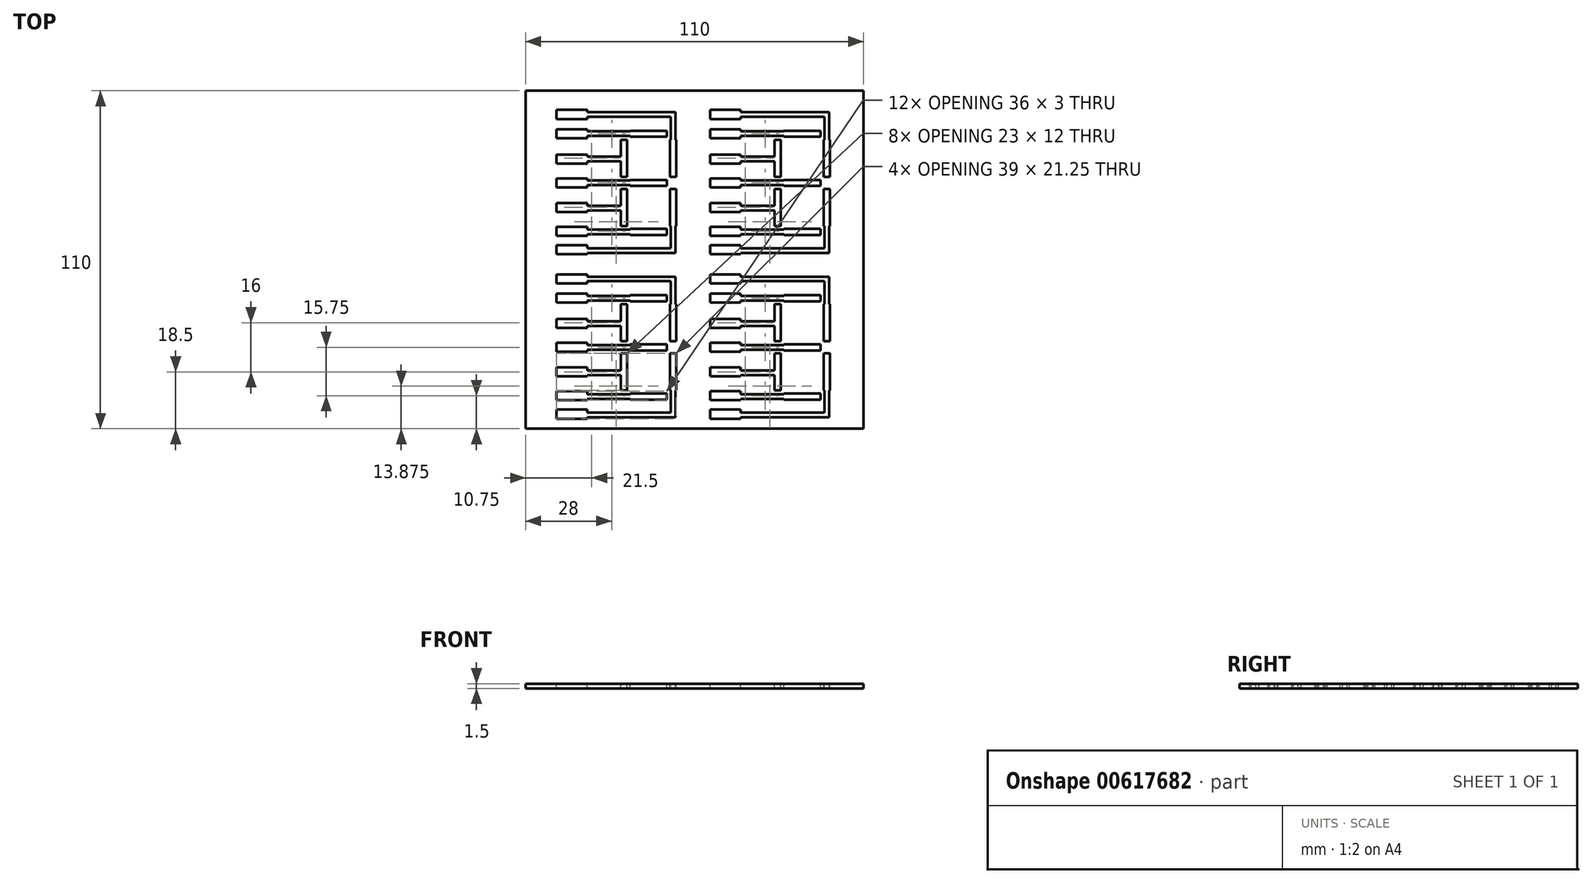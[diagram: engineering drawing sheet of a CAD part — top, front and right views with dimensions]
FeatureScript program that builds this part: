
annotation { "Feature Type Name" : "Feature", "Feature Type Description" : "" }
export const myFeature = defineFeature(function(context is Context, id is Id, definition is map)
    precondition{}
    {
        {
            var Q0;
            Q0=qCreatedBy(makeId("Top.planeOp"),FACE);
            var sketch = newSketch(context, id + "F0", { "sketchPlane" : qUnion([Q0])});
            skLineSegment(sketch, "E0.bottom", {"start": v(0, 0) * mm, "end": v(110, 0) * mm});
            skLineSegment(sketch, "E0.top", {"start": v(0, 110) * mm, "end": v(110, 110) * mm});
            skLineSegment(sketch, "E0.left", {"start": v(0, 0) * mm, "end": v(0, 110) * mm});
            skLineSegment(sketch, "E0.right", {"start": v(110, 0) * mm, "end": v(110, 110) * mm});
            skSolve(sketch);
        }
        {
            var Q0;
            Q0=qSketchRegion(id+"F0",true);
            extrude(context, id + "F1", {"entities" : qUnion([Q0]), "depth" : 1.5 * mm, "offsetDistance" : 25 * mm});
        }
        {
            var Q0;
            Q0=makeQuery(id+"F1.opExtrude","CAP_FACE",FACE,{"disambiguationData":[OSD([sQuery(id+"F0.wireOp",EDGE,"E0.bottom"),sQuery(id+"F0.wireOp",EDGE,"E0.top"),sQuery(id+"F0.wireOp",EDGE,"E0.left"),sQuery(id+"F0.wireOp",EDGE,"E0.right")])],"isStart":false});
            var sketch = newSketch(context, id + "F2", { "sketchPlane" : qUnion([Q0])});
            skLineSegment(sketch, "E1", {"start": v(50, 110) * mm, "end": v(50, 0) * mm, "construction": true});
            skLineSegment(sketch, "E2", {"start": v(100, 110) * mm, "end": v(100, 0) * mm, "construction": true});
            skLineSegment(sketch, "E3", {"start": v(0, 60) * mm, "end": v(110, 60) * mm, "construction": true});
            skLineSegment(sketch, "E4", {"start": v(0, 10) * mm, "end": v(110, 10) * mm, "construction": true});
            skSolve(sketch);
        }
        {
            var Q0;
            Q0=makeQuery(id+"F2.imprint","IMPRINT",FACE,{"disambiguationData":[TD([[makeQuery(id+"F2.imprint","IMPRINT",EDGE,{"derivedFrom":makeQuery(id+"F1.opExtrude","CAP_EDGE",EDGE,{"disambiguationData":[OSD([sQuery(id+"F0.wireOp",EDGE,"E0.bottom")])],"isStart":false})}),1.0]])]});
            var sketch = newSketch(context, id + "F3", { "sketchPlane" : qUnion([Q0])});
            skLineSegment(sketch, "E5.bottom", {"start": v(34, 97) * mm, "end": v(46, 97) * mm});
            skLineSegment(sketch, "E5.top", {"start": v(34, 95) * mm, "end": v(46, 95) * mm});
            skLineSegment(sketch, "E5.left", {"start": v(34, 97) * mm, "end": v(34, 96.75) * mm});
            skLineSegment(sketch, "E5.right", {"start": v(46, 97) * mm, "end": v(46, 95) * mm});
            skLineSegment(sketch, "E6.bottom", {"start": v(47, 94) * mm, "end": v(49, 94) * mm});
            skLineSegment(sketch, "E6.top", {"start": v(47, 82) * mm, "end": v(49, 82) * mm});
            skLineSegment(sketch, "E6.left", {"start": v(47, 94) * mm, "end": v(47, 82) * mm});
            skLineSegment(sketch, "E6.right", {"start": v(49, 94) * mm, "end": v(49, 82) * mm});
            skLineSegment(sketch, "E7.bottom", {"start": v(46, 81) * mm, "end": v(34, 81) * mm});
            skLineSegment(sketch, "E7.top", {"start": v(46, 79) * mm, "end": v(34, 79) * mm});
            skLineSegment(sketch, "E7.left", {"start": v(46, 81) * mm, "end": v(46, 79) * mm});
            skLineSegment(sketch, "E8.bottom", {"start": v(47, 78) * mm, "end": v(49, 78) * mm});
            skLineSegment(sketch, "E8.top", {"start": v(47, 66) * mm, "end": v(47.25, 66) * mm});
            skLineSegment(sketch, "E8.left", {"start": v(47, 78) * mm, "end": v(47, 66) * mm});
            skLineSegment(sketch, "E8.right", {"start": v(49, 78) * mm, "end": v(49, 66) * mm});
            skLineSegment(sketch, "E9.bottom", {"start": v(46, 65) * mm, "end": v(34, 65) * mm});
            skLineSegment(sketch, "E9.top", {"start": v(46, 63) * mm, "end": v(34, 63) * mm});
            skLineSegment(sketch, "E9.left", {"start": v(46, 65) * mm, "end": v(46, 63) * mm});
            skLineSegment(sketch, "E9.right", {"start": v(34, 65) * mm, "end": v(34, 64.75) * mm});
            skLineSegment(sketch, "E10.bottom", {"start": v(33, 66) * mm, "end": v(31, 66) * mm});
            skLineSegment(sketch, "E10.top", {"start": v(33, 78) * mm, "end": v(31, 78) * mm});
            skLineSegment(sketch, "E10.left", {"start": v(33, 66) * mm, "end": v(33, 78) * mm});
            skLineSegment(sketch, "E10.right", {"start": v(31, 66) * mm, "end": v(31, 71) * mm});
            skLineSegment(sketch, "E11.bottom", {"start": v(33, 82) * mm, "end": v(31, 82) * mm});
            skLineSegment(sketch, "E11.top", {"start": v(33, 94) * mm, "end": v(31, 94) * mm});
            skLineSegment(sketch, "E11.left", {"start": v(33, 82) * mm, "end": v(33, 94) * mm});
            skLineSegment(sketch, "E11.right", {"start": v(31, 82) * mm, "end": v(31, 87) * mm});
            skLineSegment(sketch, "E12", {"start": v(48.75, 94) * mm, "end": v(48.75, 103) * mm});
            skLineSegment(sketch, "E13", {"start": v(48.75, 103) * mm, "end": v(20, 103) * mm});
            skLineSegment(sketch, "E14", {"start": v(47.25, 94) * mm, "end": v(47.25, 101.5) * mm});
            skLineSegment(sketch, "E15", {"start": v(47.25, 101.5) * mm, "end": v(20, 101.5) * mm});
            skLineSegment(sketch, "E16", {"start": v(20, 101.5) * mm, "end": v(20, 100.75) * mm});
            skLineSegment(sketch, "E17", {"start": v(20, 100.75) * mm, "end": v(10, 100.75) * mm});
            skLineSegment(sketch, "E18", {"start": v(10, 100.75) * mm, "end": v(10, 103.75) * mm});
            skLineSegment(sketch, "E19", {"start": v(10, 103.75) * mm, "end": v(20, 103.75) * mm});
            skLineSegment(sketch, "E20", {"start": v(20, 103.75) * mm, "end": v(20, 103) * mm});
            skLineSegment(sketch, "E21", {"start": v(34, 96.75) * mm, "end": v(20, 96.75) * mm});
            skLineSegment(sketch, "E22", {"start": v(20, 96.75) * mm, "end": v(20, 97.5) * mm});
            skLineSegment(sketch, "E23", {"start": v(20, 97.5) * mm, "end": v(10, 97.5) * mm});
            skLineSegment(sketch, "E24", {"start": v(10, 97.5) * mm, "end": v(10, 94.5) * mm});
            skLineSegment(sketch, "E25", {"start": v(10, 94.5) * mm, "end": v(20, 94.5) * mm});
            skLineSegment(sketch, "E26.trimOffspring", {"start": v(34, 95.25) * mm, "end": v(34, 95) * mm});
            skLineSegment(sketch, "E27.bottom", {"start": v(31, 88.5) * mm, "end": v(20, 88.5) * mm});
            skLineSegment(sketch, "E27.top", {"start": v(31, 87) * mm, "end": v(20, 87) * mm});
            skLineSegment(sketch, "E28.bottom", {"start": v(20, 89.25) * mm, "end": v(10, 89.25) * mm});
            skLineSegment(sketch, "E28.top", {"start": v(20, 86.25) * mm, "end": v(10, 86.25) * mm});
            skLineSegment(sketch, "E28.left", {"start": v(20, 89.25) * mm, "end": v(20, 88.5) * mm});
            skLineSegment(sketch, "E28.right", {"start": v(10, 89.25) * mm, "end": v(10, 86.25) * mm});
            skLineSegment(sketch, "E29.trimOffspring", {"start": v(20, 87) * mm, "end": v(20, 86.25) * mm});
            skLineSegment(sketch, "E30.trimOffspring", {"start": v(31, 88.5) * mm, "end": v(31, 94) * mm});
            skLineSegment(sketch, "E31.bottom", {"start": v(34, 80.75) * mm, "end": v(20, 80.75) * mm});
            skLineSegment(sketch, "E31.top", {"start": v(34, 79.25) * mm, "end": v(20, 79.25) * mm});
            skLineSegment(sketch, "E32.bottom", {"start": v(20, 81.5) * mm, "end": v(10, 81.5) * mm});
            skLineSegment(sketch, "E32.top", {"start": v(20, 78.5) * mm, "end": v(10, 78.5) * mm});
            skLineSegment(sketch, "E32.left", {"start": v(20, 81.5) * mm, "end": v(20, 80.75) * mm});
            skLineSegment(sketch, "E32.right", {"start": v(10, 81.5) * mm, "end": v(10, 78.5) * mm});
            skLineSegment(sketch, "E33.trimOffspring", {"start": v(20, 79.25) * mm, "end": v(20, 78.5) * mm});
            skLineSegment(sketch, "E34.bottom", {"start": v(31, 72.5) * mm, "end": v(20, 72.5) * mm});
            skLineSegment(sketch, "E34.top", {"start": v(31, 71) * mm, "end": v(20, 71) * mm});
            skLineSegment(sketch, "E35.bottom", {"start": v(20, 73.5) * mm, "end": v(10, 73.5) * mm});
            skLineSegment(sketch, "E35.top", {"start": v(20, 70.5) * mm, "end": v(10, 70.5) * mm});
            skLineSegment(sketch, "E35.left", {"start": v(20, 73.5) * mm, "end": v(20, 72.5) * mm});
            skLineSegment(sketch, "E35.right", {"start": v(10, 73.5) * mm, "end": v(10, 70.5) * mm});
            skLineSegment(sketch, "E36.trimOffspring", {"start": v(20, 71) * mm, "end": v(20, 70.5) * mm});
            skLineSegment(sketch, "E37.trimOffspring", {"start": v(31, 72.5) * mm, "end": v(31, 78) * mm});
            skLineSegment(sketch, "E38.trimOffspring", {"start": v(34, 79.25) * mm, "end": v(34, 79) * mm});
            skLineSegment(sketch, "E39.bottom", {"start": v(34, 64.75) * mm, "end": v(20, 64.75) * mm});
            skLineSegment(sketch, "E39.top", {"start": v(34, 63.25) * mm, "end": v(20, 63.25) * mm});
            skLineSegment(sketch, "E40.bottom", {"start": v(20, 65.75) * mm, "end": v(10, 65.75) * mm});
            skLineSegment(sketch, "E40.top", {"start": v(20, 62.75) * mm, "end": v(10, 62.75) * mm});
            skLineSegment(sketch, "E40.left", {"start": v(20, 65.75) * mm, "end": v(20, 64.75) * mm});
            skLineSegment(sketch, "E40.right", {"start": v(10, 65.75) * mm, "end": v(10, 62.75) * mm});
            skLineSegment(sketch, "E41.trimOffspring", {"start": v(20, 63.25) * mm, "end": v(20, 62.75) * mm});
            skLineSegment(sketch, "E42.trimOffspring", {"start": v(34, 63.25) * mm, "end": v(34, 63) * mm});
            skLineSegment(sketch, "E43.bottom", {"start": v(47.25, 58.75) * mm, "end": v(20, 58.75) * mm});
            skLineSegment(sketch, "E43.top", {"start": v(48.75, 57.25) * mm, "end": v(20, 57.25) * mm});
            skLineSegment(sketch, "E44.bottom", {"start": v(20, 59.75) * mm, "end": v(10, 59.75) * mm});
            skLineSegment(sketch, "E44.top", {"start": v(20, 56.75) * mm, "end": v(10, 56.75) * mm});
            skLineSegment(sketch, "E44.left", {"start": v(20, 59.75) * mm, "end": v(20, 58.75) * mm});
            skLineSegment(sketch, "E44.right", {"start": v(10, 59.75) * mm, "end": v(10, 56.75) * mm});
            skLineSegment(sketch, "E45.trimOffspring", {"start": v(20, 57.25) * mm, "end": v(20, 56.75) * mm});
            skLineSegment(sketch, "E46", {"start": v(48.75, 57.25) * mm, "end": v(48.75, 66) * mm});
            skLineSegment(sketch, "E47", {"start": v(47.25, 58.75) * mm, "end": v(47.25, 66) * mm});
            skLineSegment(sketch, "E48.trimOffspring", {"start": v(48.75, 66) * mm, "end": v(49, 66) * mm});
            skLineSegment(sketch, "E49", {"start": v(34, 80.75) * mm, "end": v(34, 81) * mm});
            skLineSegment(sketch, "E50", {"start": v(34, 95.25) * mm, "end": v(20, 95.25) * mm});
            skLineSegment(sketch, "E51", {"start": v(20, 95.25) * mm, "end": v(20, 94.5) * mm});
            skLineSegment(sketch, "E52.0.1.0", {"start": v(10, 44) * mm, "end": v(10, 41) * mm});
            skLineSegment(sketch, "E52.0.1.1", {"start": v(34, 27.25) * mm, "end": v(20, 27.25) * mm});
            skLineSegment(sketch, "E52.0.1.2", {"start": v(31, 19) * mm, "end": v(31, 24.5) * mm});
            skLineSegment(sketch, "E52.0.1.3", {"start": v(47.25, 5.25) * mm, "end": v(20, 5.25) * mm});
            skLineSegment(sketch, "E52.0.1.4", {"start": v(31, 17.5) * mm, "end": v(20, 17.5) * mm});
            skLineSegment(sketch, "E52.0.1.5", {"start": v(20, 17) * mm, "end": v(10, 17) * mm});
            skLineSegment(sketch, "E52.0.1.6", {"start": v(34, 25.75) * mm, "end": v(20, 25.75) * mm});
            skLineSegment(sketch, "E52.0.1.7", {"start": v(31, 19) * mm, "end": v(20, 19) * mm});
            skLineSegment(sketch, "E52.0.1.8", {"start": v(20, 25) * mm, "end": v(10, 25) * mm});
            skLineSegment(sketch, "E52.0.1.9", {"start": v(47, 24.5) * mm, "end": v(47, 12.5) * mm});
            skLineSegment(sketch, "E52.0.1.10", {"start": v(20, 20) * mm, "end": v(10, 20) * mm});
            skLineSegment(sketch, "E52.0.1.11", {"start": v(10, 47.25) * mm, "end": v(10, 50.25) * mm});
            skLineSegment(sketch, "E52.0.1.12", {"start": v(31, 12.5) * mm, "end": v(31, 17.5) * mm});
            skLineSegment(sketch, "E52.0.1.13", {"start": v(10, 12.25) * mm, "end": v(10, 9.25) * mm});
            skLineSegment(sketch, "E52.0.1.14", {"start": v(10, 41) * mm, "end": v(20, 41) * mm});
            skLineSegment(sketch, "E52.0.1.15", {"start": v(10, 50.25) * mm, "end": v(20, 50.25) * mm});
            skLineSegment(sketch, "E52.0.1.16", {"start": v(10, 20) * mm, "end": v(10, 17) * mm});
            skLineSegment(sketch, "E52.0.1.17", {"start": v(34, 9.75) * mm, "end": v(20, 9.75) * mm});
            skLineSegment(sketch, "E52.0.1.18", {"start": v(48.75, 49.5) * mm, "end": v(20, 49.5) * mm});
            skLineSegment(sketch, "E52.0.1.19", {"start": v(34, 41.75) * mm, "end": v(20, 41.75) * mm});
            skLineSegment(sketch, "E52.0.1.20", {"start": v(47.25, 48) * mm, "end": v(20, 48) * mm});
            skLineSegment(sketch, "E52.0.1.21", {"start": v(48.75, 40.5) * mm, "end": v(48.75, 49.5) * mm});
            skLineSegment(sketch, "E52.0.1.22", {"start": v(20, 12.25) * mm, "end": v(10, 12.25) * mm});
            skLineSegment(sketch, "E52.0.1.23", {"start": v(10, 6.25) * mm, "end": v(10, 3.25) * mm});
            skLineSegment(sketch, "E52.0.1.24", {"start": v(33, 28.5) * mm, "end": v(33, 40.5) * mm});
            skLineSegment(sketch, "E52.0.1.25", {"start": v(34, 11.25) * mm, "end": v(20, 11.25) * mm});
            skLineSegment(sketch, "E52.0.1.26", {"start": v(20, 47.25) * mm, "end": v(10, 47.25) * mm});
            skLineSegment(sketch, "E52.0.1.27", {"start": v(20, 9.25) * mm, "end": v(10, 9.25) * mm});
            skLineSegment(sketch, "E52.0.1.28", {"start": v(34, 43.25) * mm, "end": v(20, 43.25) * mm});
            skLineSegment(sketch, "E52.0.1.29", {"start": v(33, 12.5) * mm, "end": v(33, 24.5) * mm});
            skLineSegment(sketch, "E52.0.1.30", {"start": v(47, 40.5) * mm, "end": v(47, 28.5) * mm});
            skLineSegment(sketch, "E52.0.1.31", {"start": v(10, 35.75) * mm, "end": v(10, 32.75) * mm});
            skLineSegment(sketch, "E52.0.1.32", {"start": v(20, 6.25) * mm, "end": v(10, 6.25) * mm});
            skLineSegment(sketch, "E52.0.1.33", {"start": v(34, 43.5) * mm, "end": v(46, 43.5) * mm});
            skLineSegment(sketch, "E52.0.1.34", {"start": v(49, 40.5) * mm, "end": v(49, 28.5) * mm});
            skLineSegment(sketch, "E52.0.1.35", {"start": v(31, 35) * mm, "end": v(20, 35) * mm});
            skLineSegment(sketch, "E52.0.1.36", {"start": v(46, 27.5) * mm, "end": v(34, 27.5) * mm});
            skLineSegment(sketch, "E52.0.1.37", {"start": v(48.75, 3.75) * mm, "end": v(48.75, 12.5) * mm});
            skLineSegment(sketch, "E52.0.1.38", {"start": v(46, 25.5) * mm, "end": v(34, 25.5) * mm});
            skLineSegment(sketch, "E52.0.1.39", {"start": v(31, 33.5) * mm, "end": v(20, 33.5) * mm});
            skLineSegment(sketch, "E52.0.1.40", {"start": v(47.25, 40.5) * mm, "end": v(47.25, 48) * mm});
            skLineSegment(sketch, "E52.0.1.41", {"start": v(48.75, 3.75) * mm, "end": v(20, 3.75) * mm});
            skLineSegment(sketch, "E52.0.1.42", {"start": v(49, 24.5) * mm, "end": v(49, 12.5) * mm});
            skLineSegment(sketch, "E52.0.1.43", {"start": v(10, 28) * mm, "end": v(10, 25) * mm});
            skLineSegment(sketch, "E52.0.1.44", {"start": v(34, 41.5) * mm, "end": v(46, 41.5) * mm});
            skLineSegment(sketch, "E52.0.1.45", {"start": v(20, 28) * mm, "end": v(10, 28) * mm});
            skLineSegment(sketch, "E52.0.1.46", {"start": v(46, 9.5) * mm, "end": v(34, 9.5) * mm});
            skLineSegment(sketch, "E52.0.1.47", {"start": v(20, 3.25) * mm, "end": v(10, 3.25) * mm});
            skLineSegment(sketch, "E52.0.1.48", {"start": v(20, 32.75) * mm, "end": v(10, 32.75) * mm});
            skLineSegment(sketch, "E52.0.1.49", {"start": v(47.25, 5.25) * mm, "end": v(47.25, 12.5) * mm});
            skLineSegment(sketch, "E52.0.1.50", {"start": v(20, 35.75) * mm, "end": v(10, 35.75) * mm});
            skLineSegment(sketch, "E52.0.1.51", {"start": v(46, 11.5) * mm, "end": v(34, 11.5) * mm});
            skLineSegment(sketch, "E52.0.1.52", {"start": v(20, 44) * mm, "end": v(10, 44) * mm});
            skLineSegment(sketch, "E52.0.1.53", {"start": v(31, 35) * mm, "end": v(31, 40.5) * mm});
            skLineSegment(sketch, "E52.0.1.54", {"start": v(31, 28.5) * mm, "end": v(31, 33.5) * mm});
            skLineSegment(sketch, "E52.0.1.55", {"start": v(33, 24.5) * mm, "end": v(31, 24.5) * mm});
            skLineSegment(sketch, "E52.0.1.56", {"start": v(20, 20) * mm, "end": v(20, 19) * mm});
            skLineSegment(sketch, "E52.0.1.57", {"start": v(47, 28.5) * mm, "end": v(49, 28.5) * mm});
            skLineSegment(sketch, "E52.0.1.58", {"start": v(20, 33.5) * mm, "end": v(20, 32.75) * mm});
            skLineSegment(sketch, "E52.0.1.59", {"start": v(20, 6.25) * mm, "end": v(20, 5.25) * mm});
            skLineSegment(sketch, "E52.0.1.60", {"start": v(33, 40.5) * mm, "end": v(31, 40.5) * mm});
            skLineSegment(sketch, "E52.0.1.61", {"start": v(20, 12.25) * mm, "end": v(20, 11.25) * mm});
            skLineSegment(sketch, "E52.0.1.62", {"start": v(47, 24.5) * mm, "end": v(49, 24.5) * mm});
            skLineSegment(sketch, "E52.0.1.63", {"start": v(46, 43.5) * mm, "end": v(46, 41.5) * mm});
            skLineSegment(sketch, "E52.0.1.64", {"start": v(46, 11.5) * mm, "end": v(46, 9.5) * mm});
            skLineSegment(sketch, "E52.0.1.65", {"start": v(46, 27.5) * mm, "end": v(46, 25.5) * mm});
            skLineSegment(sketch, "E52.0.1.66", {"start": v(33, 28.5) * mm, "end": v(31, 28.5) * mm});
            skLineSegment(sketch, "E52.0.1.67", {"start": v(34, 27.25) * mm, "end": v(34, 27.5) * mm});
            skLineSegment(sketch, "E52.0.1.68", {"start": v(34, 43.5) * mm, "end": v(34, 43.25) * mm});
            skLineSegment(sketch, "E52.0.1.69", {"start": v(20, 28) * mm, "end": v(20, 27.25) * mm});
            skLineSegment(sketch, "E52.0.1.70", {"start": v(20, 3.75) * mm, "end": v(20, 3.25) * mm});
            skLineSegment(sketch, "E52.0.1.71", {"start": v(20, 9.75) * mm, "end": v(20, 9.25) * mm});
            skLineSegment(sketch, "E52.0.1.72", {"start": v(20, 50.25) * mm, "end": v(20, 49.5) * mm});
            skLineSegment(sketch, "E52.0.1.73", {"start": v(20, 17.5) * mm, "end": v(20, 17) * mm});
            skLineSegment(sketch, "E52.0.1.74", {"start": v(47, 40.5) * mm, "end": v(49, 40.5) * mm});
            skLineSegment(sketch, "E52.0.1.75", {"start": v(20, 35.75) * mm, "end": v(20, 35) * mm});
            skLineSegment(sketch, "E52.0.1.76", {"start": v(20, 48) * mm, "end": v(20, 47.25) * mm});
            skLineSegment(sketch, "E52.0.1.77", {"start": v(33, 12.5) * mm, "end": v(31, 12.5) * mm});
            skLineSegment(sketch, "E52.0.1.78", {"start": v(20, 43.25) * mm, "end": v(20, 44) * mm});
            skLineSegment(sketch, "E52.0.1.79", {"start": v(48.75, 12.5) * mm, "end": v(49, 12.5) * mm});
            skLineSegment(sketch, "E52.0.1.80", {"start": v(34, 25.75) * mm, "end": v(34, 25.5) * mm});
            skLineSegment(sketch, "E52.0.1.81", {"start": v(47, 12.5) * mm, "end": v(47.25, 12.5) * mm});
            skLineSegment(sketch, "E52.0.1.82", {"start": v(20, 25.75) * mm, "end": v(20, 25) * mm});
            skLineSegment(sketch, "E52.0.1.83", {"start": v(20, 41.75) * mm, "end": v(20, 41) * mm});
            skLineSegment(sketch, "E52.0.1.84", {"start": v(34, 41.75) * mm, "end": v(34, 41.5) * mm});
            skLineSegment(sketch, "E52.0.1.85", {"start": v(34, 11.5) * mm, "end": v(34, 11.25) * mm});
            skLineSegment(sketch, "E52.0.1.86", {"start": v(34, 9.75) * mm, "end": v(34, 9.5) * mm});
            skLineSegment(sketch, "E52.1.0.0", {"start": v(60, 97.5) * mm, "end": v(60, 94.5) * mm});
            skLineSegment(sketch, "E52.1.0.1", {"start": v(84, 80.75) * mm, "end": v(70, 80.75) * mm});
            skLineSegment(sketch, "E52.1.0.2", {"start": v(81, 72.5) * mm, "end": v(81, 78) * mm});
            skLineSegment(sketch, "E52.1.0.3", {"start": v(97.25, 58.75) * mm, "end": v(70, 58.75) * mm});
            skLineSegment(sketch, "E52.1.0.4", {"start": v(81, 71) * mm, "end": v(70, 71) * mm});
            skLineSegment(sketch, "E52.1.0.5", {"start": v(70, 70.5) * mm, "end": v(60, 70.5) * mm});
            skLineSegment(sketch, "E52.1.0.6", {"start": v(84, 79.25) * mm, "end": v(70, 79.25) * mm});
            skLineSegment(sketch, "E52.1.0.7", {"start": v(81, 72.5) * mm, "end": v(70, 72.5) * mm});
            skLineSegment(sketch, "E52.1.0.8", {"start": v(70, 78.5) * mm, "end": v(60, 78.5) * mm});
            skLineSegment(sketch, "E52.1.0.9", {"start": v(97, 78) * mm, "end": v(97, 66) * mm});
            skLineSegment(sketch, "E52.1.0.10", {"start": v(70, 73.5) * mm, "end": v(60, 73.5) * mm});
            skLineSegment(sketch, "E52.1.0.11", {"start": v(60, 100.75) * mm, "end": v(60, 103.75) * mm});
            skLineSegment(sketch, "E52.1.0.12", {"start": v(81, 66) * mm, "end": v(81, 71) * mm});
            skLineSegment(sketch, "E52.1.0.13", {"start": v(60, 65.75) * mm, "end": v(60, 62.75) * mm});
            skLineSegment(sketch, "E52.1.0.14", {"start": v(60, 94.5) * mm, "end": v(70, 94.5) * mm});
            skLineSegment(sketch, "E52.1.0.15", {"start": v(60, 103.75) * mm, "end": v(70, 103.75) * mm});
            skLineSegment(sketch, "E52.1.0.16", {"start": v(60, 73.5) * mm, "end": v(60, 70.5) * mm});
            skLineSegment(sketch, "E52.1.0.17", {"start": v(84, 63.25) * mm, "end": v(70, 63.25) * mm});
            skLineSegment(sketch, "E52.1.0.18", {"start": v(98.75, 103) * mm, "end": v(70, 103) * mm});
            skLineSegment(sketch, "E52.1.0.19", {"start": v(84, 95.25) * mm, "end": v(70, 95.25) * mm});
            skLineSegment(sketch, "E52.1.0.20", {"start": v(97.25, 101.5) * mm, "end": v(70, 101.5) * mm});
            skLineSegment(sketch, "E52.1.0.21", {"start": v(98.75, 94) * mm, "end": v(98.75, 103) * mm});
            skLineSegment(sketch, "E52.1.0.22", {"start": v(70, 65.75) * mm, "end": v(60, 65.75) * mm});
            skLineSegment(sketch, "E52.1.0.23", {"start": v(60, 59.75) * mm, "end": v(60, 56.75) * mm});
            skLineSegment(sketch, "E52.1.0.24", {"start": v(83, 82) * mm, "end": v(83, 94) * mm});
            skLineSegment(sketch, "E52.1.0.25", {"start": v(84, 64.75) * mm, "end": v(70, 64.75) * mm});
            skLineSegment(sketch, "E52.1.0.26", {"start": v(70, 100.75) * mm, "end": v(60, 100.75) * mm});
            skLineSegment(sketch, "E52.1.0.27", {"start": v(70, 62.75) * mm, "end": v(60, 62.75) * mm});
            skLineSegment(sketch, "E52.1.0.28", {"start": v(84, 96.75) * mm, "end": v(70, 96.75) * mm});
            skLineSegment(sketch, "E52.1.0.29", {"start": v(83, 66) * mm, "end": v(83, 78) * mm});
            skLineSegment(sketch, "E52.1.0.30", {"start": v(97, 94) * mm, "end": v(97, 82) * mm});
            skLineSegment(sketch, "E52.1.0.31", {"start": v(60, 89.25) * mm, "end": v(60, 86.25) * mm});
            skLineSegment(sketch, "E52.1.0.32", {"start": v(70, 59.75) * mm, "end": v(60, 59.75) * mm});
            skLineSegment(sketch, "E52.1.0.33", {"start": v(84, 97) * mm, "end": v(96, 97) * mm});
            skLineSegment(sketch, "E52.1.0.34", {"start": v(99, 94) * mm, "end": v(99, 82) * mm});
            skLineSegment(sketch, "E52.1.0.35", {"start": v(81, 88.5) * mm, "end": v(70, 88.5) * mm});
            skLineSegment(sketch, "E52.1.0.36", {"start": v(96, 81) * mm, "end": v(84, 81) * mm});
            skLineSegment(sketch, "E52.1.0.37", {"start": v(98.75, 57.25) * mm, "end": v(98.75, 66) * mm});
            skLineSegment(sketch, "E52.1.0.38", {"start": v(96, 79) * mm, "end": v(84, 79) * mm});
            skLineSegment(sketch, "E52.1.0.39", {"start": v(81, 87) * mm, "end": v(70, 87) * mm});
            skLineSegment(sketch, "E52.1.0.40", {"start": v(97.25, 94) * mm, "end": v(97.25, 101.5) * mm});
            skLineSegment(sketch, "E52.1.0.41", {"start": v(98.75, 57.25) * mm, "end": v(70, 57.25) * mm});
            skLineSegment(sketch, "E52.1.0.42", {"start": v(99, 78) * mm, "end": v(99, 66) * mm});
            skLineSegment(sketch, "E52.1.0.43", {"start": v(60, 81.5) * mm, "end": v(60, 78.5) * mm});
            skLineSegment(sketch, "E52.1.0.44", {"start": v(84, 95) * mm, "end": v(96, 95) * mm});
            skLineSegment(sketch, "E52.1.0.45", {"start": v(70, 81.5) * mm, "end": v(60, 81.5) * mm});
            skLineSegment(sketch, "E52.1.0.46", {"start": v(96, 63) * mm, "end": v(84, 63) * mm});
            skLineSegment(sketch, "E52.1.0.47", {"start": v(70, 56.75) * mm, "end": v(60, 56.75) * mm});
            skLineSegment(sketch, "E52.1.0.48", {"start": v(70, 86.25) * mm, "end": v(60, 86.25) * mm});
            skLineSegment(sketch, "E52.1.0.49", {"start": v(97.25, 58.75) * mm, "end": v(97.25, 66) * mm});
            skLineSegment(sketch, "E52.1.0.50", {"start": v(70, 89.25) * mm, "end": v(60, 89.25) * mm});
            skLineSegment(sketch, "E52.1.0.51", {"start": v(96, 65) * mm, "end": v(84, 65) * mm});
            skLineSegment(sketch, "E52.1.0.52", {"start": v(70, 97.5) * mm, "end": v(60, 97.5) * mm});
            skLineSegment(sketch, "E52.1.0.53", {"start": v(81, 88.5) * mm, "end": v(81, 94) * mm});
            skLineSegment(sketch, "E52.1.0.54", {"start": v(81, 82) * mm, "end": v(81, 87) * mm});
            skLineSegment(sketch, "E52.1.0.55", {"start": v(83, 78) * mm, "end": v(81, 78) * mm});
            skLineSegment(sketch, "E52.1.0.56", {"start": v(70, 73.5) * mm, "end": v(70, 72.5) * mm});
            skLineSegment(sketch, "E52.1.0.57", {"start": v(97, 82) * mm, "end": v(99, 82) * mm});
            skLineSegment(sketch, "E52.1.0.58", {"start": v(70, 87) * mm, "end": v(70, 86.25) * mm});
            skLineSegment(sketch, "E52.1.0.59", {"start": v(70, 59.75) * mm, "end": v(70, 58.75) * mm});
            skLineSegment(sketch, "E52.1.0.60", {"start": v(83, 94) * mm, "end": v(81, 94) * mm});
            skLineSegment(sketch, "E52.1.0.61", {"start": v(70, 65.75) * mm, "end": v(70, 64.75) * mm});
            skLineSegment(sketch, "E52.1.0.62", {"start": v(97, 78) * mm, "end": v(99, 78) * mm});
            skLineSegment(sketch, "E52.1.0.63", {"start": v(96, 97) * mm, "end": v(96, 95) * mm});
            skLineSegment(sketch, "E52.1.0.64", {"start": v(96, 65) * mm, "end": v(96, 63) * mm});
            skLineSegment(sketch, "E52.1.0.65", {"start": v(96, 81) * mm, "end": v(96, 79) * mm});
            skLineSegment(sketch, "E52.1.0.66", {"start": v(83, 82) * mm, "end": v(81, 82) * mm});
            skLineSegment(sketch, "E52.1.0.67", {"start": v(84, 80.75) * mm, "end": v(84, 81) * mm});
            skLineSegment(sketch, "E52.1.0.68", {"start": v(84, 97) * mm, "end": v(84, 96.75) * mm});
            skLineSegment(sketch, "E52.1.0.69", {"start": v(70, 81.5) * mm, "end": v(70, 80.75) * mm});
            skLineSegment(sketch, "E52.1.0.70", {"start": v(70, 57.25) * mm, "end": v(70, 56.75) * mm});
            skLineSegment(sketch, "E52.1.0.71", {"start": v(70, 63.25) * mm, "end": v(70, 62.75) * mm});
            skLineSegment(sketch, "E52.1.0.72", {"start": v(70, 103.75) * mm, "end": v(70, 103) * mm});
            skLineSegment(sketch, "E52.1.0.73", {"start": v(70, 71) * mm, "end": v(70, 70.5) * mm});
            skLineSegment(sketch, "E52.1.0.74", {"start": v(97, 94) * mm, "end": v(99, 94) * mm});
            skLineSegment(sketch, "E52.1.0.75", {"start": v(70, 89.25) * mm, "end": v(70, 88.5) * mm});
            skLineSegment(sketch, "E52.1.0.76", {"start": v(70, 101.5) * mm, "end": v(70, 100.75) * mm});
            skLineSegment(sketch, "E52.1.0.77", {"start": v(83, 66) * mm, "end": v(81, 66) * mm});
            skLineSegment(sketch, "E52.1.0.78", {"start": v(70, 96.75) * mm, "end": v(70, 97.5) * mm});
            skLineSegment(sketch, "E52.1.0.79", {"start": v(98.75, 66) * mm, "end": v(99, 66) * mm});
            skLineSegment(sketch, "E52.1.0.80", {"start": v(84, 79.25) * mm, "end": v(84, 79) * mm});
            skLineSegment(sketch, "E52.1.0.81", {"start": v(97, 66) * mm, "end": v(97.25, 66) * mm});
            skLineSegment(sketch, "E52.1.0.82", {"start": v(70, 79.25) * mm, "end": v(70, 78.5) * mm});
            skLineSegment(sketch, "E52.1.0.83", {"start": v(70, 95.25) * mm, "end": v(70, 94.5) * mm});
            skLineSegment(sketch, "E52.1.0.84", {"start": v(84, 95.25) * mm, "end": v(84, 95) * mm});
            skLineSegment(sketch, "E52.1.0.85", {"start": v(84, 65) * mm, "end": v(84, 64.75) * mm});
            skLineSegment(sketch, "E52.1.0.86", {"start": v(84, 63.25) * mm, "end": v(84, 63) * mm});
            skLineSegment(sketch, "E52.1.1.0", {"start": v(60, 44) * mm, "end": v(60, 41) * mm});
            skLineSegment(sketch, "E52.1.1.1", {"start": v(84, 27.25) * mm, "end": v(70, 27.25) * mm});
            skLineSegment(sketch, "E52.1.1.2", {"start": v(81, 19) * mm, "end": v(81, 24.5) * mm});
            skLineSegment(sketch, "E52.1.1.3", {"start": v(97.25, 5.25) * mm, "end": v(70, 5.25) * mm});
            skLineSegment(sketch, "E52.1.1.4", {"start": v(81, 17.5) * mm, "end": v(70, 17.5) * mm});
            skLineSegment(sketch, "E52.1.1.5", {"start": v(70, 17) * mm, "end": v(60, 17) * mm});
            skLineSegment(sketch, "E52.1.1.6", {"start": v(84, 25.75) * mm, "end": v(70, 25.75) * mm});
            skLineSegment(sketch, "E52.1.1.7", {"start": v(81, 19) * mm, "end": v(70, 19) * mm});
            skLineSegment(sketch, "E52.1.1.8", {"start": v(70, 25) * mm, "end": v(60, 25) * mm});
            skLineSegment(sketch, "E52.1.1.9", {"start": v(97, 24.5) * mm, "end": v(97, 12.5) * mm});
            skLineSegment(sketch, "E52.1.1.10", {"start": v(70, 20) * mm, "end": v(60, 20) * mm});
            skLineSegment(sketch, "E52.1.1.11", {"start": v(60, 47.25) * mm, "end": v(60, 50.25) * mm});
            skLineSegment(sketch, "E52.1.1.12", {"start": v(81, 12.5) * mm, "end": v(81, 17.5) * mm});
            skLineSegment(sketch, "E52.1.1.13", {"start": v(60, 12.25) * mm, "end": v(60, 9.25) * mm});
            skLineSegment(sketch, "E52.1.1.14", {"start": v(60, 41) * mm, "end": v(70, 41) * mm});
            skLineSegment(sketch, "E52.1.1.15", {"start": v(60, 50.25) * mm, "end": v(70, 50.25) * mm});
            skLineSegment(sketch, "E52.1.1.16", {"start": v(60, 20) * mm, "end": v(60, 17) * mm});
            skLineSegment(sketch, "E52.1.1.17", {"start": v(84, 9.75) * mm, "end": v(70, 9.75) * mm});
            skLineSegment(sketch, "E52.1.1.18", {"start": v(98.75, 49.5) * mm, "end": v(70, 49.5) * mm});
            skLineSegment(sketch, "E52.1.1.19", {"start": v(84, 41.75) * mm, "end": v(70, 41.75) * mm});
            skLineSegment(sketch, "E52.1.1.20", {"start": v(97.25, 48) * mm, "end": v(70, 48) * mm});
            skLineSegment(sketch, "E52.1.1.21", {"start": v(98.75, 40.5) * mm, "end": v(98.75, 49.5) * mm});
            skLineSegment(sketch, "E52.1.1.22", {"start": v(70, 12.25) * mm, "end": v(60, 12.25) * mm});
            skLineSegment(sketch, "E52.1.1.23", {"start": v(60, 6.25) * mm, "end": v(60, 3.25) * mm});
            skLineSegment(sketch, "E52.1.1.24", {"start": v(83, 28.5) * mm, "end": v(83, 40.5) * mm});
            skLineSegment(sketch, "E52.1.1.25", {"start": v(84, 11.25) * mm, "end": v(70, 11.25) * mm});
            skLineSegment(sketch, "E52.1.1.26", {"start": v(70, 47.25) * mm, "end": v(60, 47.25) * mm});
            skLineSegment(sketch, "E52.1.1.27", {"start": v(70, 9.25) * mm, "end": v(60, 9.25) * mm});
            skLineSegment(sketch, "E52.1.1.28", {"start": v(84, 43.25) * mm, "end": v(70, 43.25) * mm});
            skLineSegment(sketch, "E52.1.1.29", {"start": v(83, 12.5) * mm, "end": v(83, 24.5) * mm});
            skLineSegment(sketch, "E52.1.1.30", {"start": v(97, 40.5) * mm, "end": v(97, 28.5) * mm});
            skLineSegment(sketch, "E52.1.1.31", {"start": v(60, 35.75) * mm, "end": v(60, 32.75) * mm});
            skLineSegment(sketch, "E52.1.1.32", {"start": v(70, 6.25) * mm, "end": v(60, 6.25) * mm});
            skLineSegment(sketch, "E52.1.1.33", {"start": v(84, 43.5) * mm, "end": v(96, 43.5) * mm});
            skLineSegment(sketch, "E52.1.1.34", {"start": v(99, 40.5) * mm, "end": v(99, 28.5) * mm});
            skLineSegment(sketch, "E52.1.1.35", {"start": v(81, 35) * mm, "end": v(70, 35) * mm});
            skLineSegment(sketch, "E52.1.1.36", {"start": v(96, 27.5) * mm, "end": v(84, 27.5) * mm});
            skLineSegment(sketch, "E52.1.1.37", {"start": v(98.75, 3.75) * mm, "end": v(98.75, 12.5) * mm});
            skLineSegment(sketch, "E52.1.1.38", {"start": v(96, 25.5) * mm, "end": v(84, 25.5) * mm});
            skLineSegment(sketch, "E52.1.1.39", {"start": v(81, 33.5) * mm, "end": v(70, 33.5) * mm});
            skLineSegment(sketch, "E52.1.1.40", {"start": v(97.25, 40.5) * mm, "end": v(97.25, 48) * mm});
            skLineSegment(sketch, "E52.1.1.41", {"start": v(98.75, 3.75) * mm, "end": v(70, 3.75) * mm});
            skLineSegment(sketch, "E52.1.1.42", {"start": v(99, 24.5) * mm, "end": v(99, 12.5) * mm});
            skLineSegment(sketch, "E52.1.1.43", {"start": v(60, 28) * mm, "end": v(60, 25) * mm});
            skLineSegment(sketch, "E52.1.1.44", {"start": v(84, 41.5) * mm, "end": v(96, 41.5) * mm});
            skLineSegment(sketch, "E52.1.1.45", {"start": v(70, 28) * mm, "end": v(60, 28) * mm});
            skLineSegment(sketch, "E52.1.1.46", {"start": v(96, 9.5) * mm, "end": v(84, 9.5) * mm});
            skLineSegment(sketch, "E52.1.1.47", {"start": v(70, 3.25) * mm, "end": v(60, 3.25) * mm});
            skLineSegment(sketch, "E52.1.1.48", {"start": v(70, 32.75) * mm, "end": v(60, 32.75) * mm});
            skLineSegment(sketch, "E52.1.1.49", {"start": v(97.25, 5.25) * mm, "end": v(97.25, 12.5) * mm});
            skLineSegment(sketch, "E52.1.1.50", {"start": v(70, 35.75) * mm, "end": v(60, 35.75) * mm});
            skLineSegment(sketch, "E52.1.1.51", {"start": v(96, 11.5) * mm, "end": v(84, 11.5) * mm});
            skLineSegment(sketch, "E52.1.1.52", {"start": v(70, 44) * mm, "end": v(60, 44) * mm});
            skLineSegment(sketch, "E52.1.1.53", {"start": v(81, 35) * mm, "end": v(81, 40.5) * mm});
            skLineSegment(sketch, "E52.1.1.54", {"start": v(81, 28.5) * mm, "end": v(81, 33.5) * mm});
            skLineSegment(sketch, "E52.1.1.55", {"start": v(83, 24.5) * mm, "end": v(81, 24.5) * mm});
            skLineSegment(sketch, "E52.1.1.56", {"start": v(70, 20) * mm, "end": v(70, 19) * mm});
            skLineSegment(sketch, "E52.1.1.57", {"start": v(97, 28.5) * mm, "end": v(99, 28.5) * mm});
            skLineSegment(sketch, "E52.1.1.58", {"start": v(70, 33.5) * mm, "end": v(70, 32.75) * mm});
            skLineSegment(sketch, "E52.1.1.59", {"start": v(70, 6.25) * mm, "end": v(70, 5.25) * mm});
            skLineSegment(sketch, "E52.1.1.60", {"start": v(83, 40.5) * mm, "end": v(81, 40.5) * mm});
            skLineSegment(sketch, "E52.1.1.61", {"start": v(70, 12.25) * mm, "end": v(70, 11.25) * mm});
            skLineSegment(sketch, "E52.1.1.62", {"start": v(97, 24.5) * mm, "end": v(99, 24.5) * mm});
            skLineSegment(sketch, "E52.1.1.63", {"start": v(96, 43.5) * mm, "end": v(96, 41.5) * mm});
            skLineSegment(sketch, "E52.1.1.64", {"start": v(96, 11.5) * mm, "end": v(96, 9.5) * mm});
            skLineSegment(sketch, "E52.1.1.65", {"start": v(96, 27.5) * mm, "end": v(96, 25.5) * mm});
            skLineSegment(sketch, "E52.1.1.66", {"start": v(83, 28.5) * mm, "end": v(81, 28.5) * mm});
            skLineSegment(sketch, "E52.1.1.67", {"start": v(84, 27.25) * mm, "end": v(84, 27.5) * mm});
            skLineSegment(sketch, "E52.1.1.68", {"start": v(84, 43.5) * mm, "end": v(84, 43.25) * mm});
            skLineSegment(sketch, "E52.1.1.69", {"start": v(70, 28) * mm, "end": v(70, 27.25) * mm});
            skLineSegment(sketch, "E52.1.1.70", {"start": v(70, 3.75) * mm, "end": v(70, 3.25) * mm});
            skLineSegment(sketch, "E52.1.1.71", {"start": v(70, 9.75) * mm, "end": v(70, 9.25) * mm});
            skLineSegment(sketch, "E52.1.1.72", {"start": v(70, 50.25) * mm, "end": v(70, 49.5) * mm});
            skLineSegment(sketch, "E52.1.1.73", {"start": v(70, 17.5) * mm, "end": v(70, 17) * mm});
            skLineSegment(sketch, "E52.1.1.74", {"start": v(97, 40.5) * mm, "end": v(99, 40.5) * mm});
            skLineSegment(sketch, "E52.1.1.75", {"start": v(70, 35.75) * mm, "end": v(70, 35) * mm});
            skLineSegment(sketch, "E52.1.1.76", {"start": v(70, 48) * mm, "end": v(70, 47.25) * mm});
            skLineSegment(sketch, "E52.1.1.77", {"start": v(83, 12.5) * mm, "end": v(81, 12.5) * mm});
            skLineSegment(sketch, "E52.1.1.78", {"start": v(70, 43.25) * mm, "end": v(70, 44) * mm});
            skLineSegment(sketch, "E52.1.1.79", {"start": v(98.75, 12.5) * mm, "end": v(99, 12.5) * mm});
            skLineSegment(sketch, "E52.1.1.80", {"start": v(84, 25.75) * mm, "end": v(84, 25.5) * mm});
            skLineSegment(sketch, "E52.1.1.81", {"start": v(97, 12.5) * mm, "end": v(97.25, 12.5) * mm});
            skLineSegment(sketch, "E52.1.1.82", {"start": v(70, 25.75) * mm, "end": v(70, 25) * mm});
            skLineSegment(sketch, "E52.1.1.83", {"start": v(70, 41.75) * mm, "end": v(70, 41) * mm});
            skLineSegment(sketch, "E52.1.1.84", {"start": v(84, 41.75) * mm, "end": v(84, 41.5) * mm});
            skLineSegment(sketch, "E52.1.1.85", {"start": v(84, 11.5) * mm, "end": v(84, 11.25) * mm});
            skLineSegment(sketch, "E52.1.1.86", {"start": v(84, 9.75) * mm, "end": v(84, 9.5) * mm});
            skLineSegment(sketch, "E52.direction1", {"start": v(10, 56.75) * mm, "end": v(60, 56.75) * mm, "construction": true});
            skLineSegment(sketch, "E52.direction2", {"start": v(10, 56.75) * mm, "end": v(10, 3.25) * mm, "construction": true});
            skSolve(sketch);
        }
        {
            var Q0;
            Q0=qSketchRegion(id+"F3",true);
            extrude(context, id + "F4", {"entities" : qUnion([Q0]), "operationType" : NewBodyOperationType.REMOVE, "endBound" : BoundingType.THROUGH_ALL, "oppositeDirection" : true, "depth" : 25 * mm, "offsetDistance" : 25 * mm});
        }
    });
